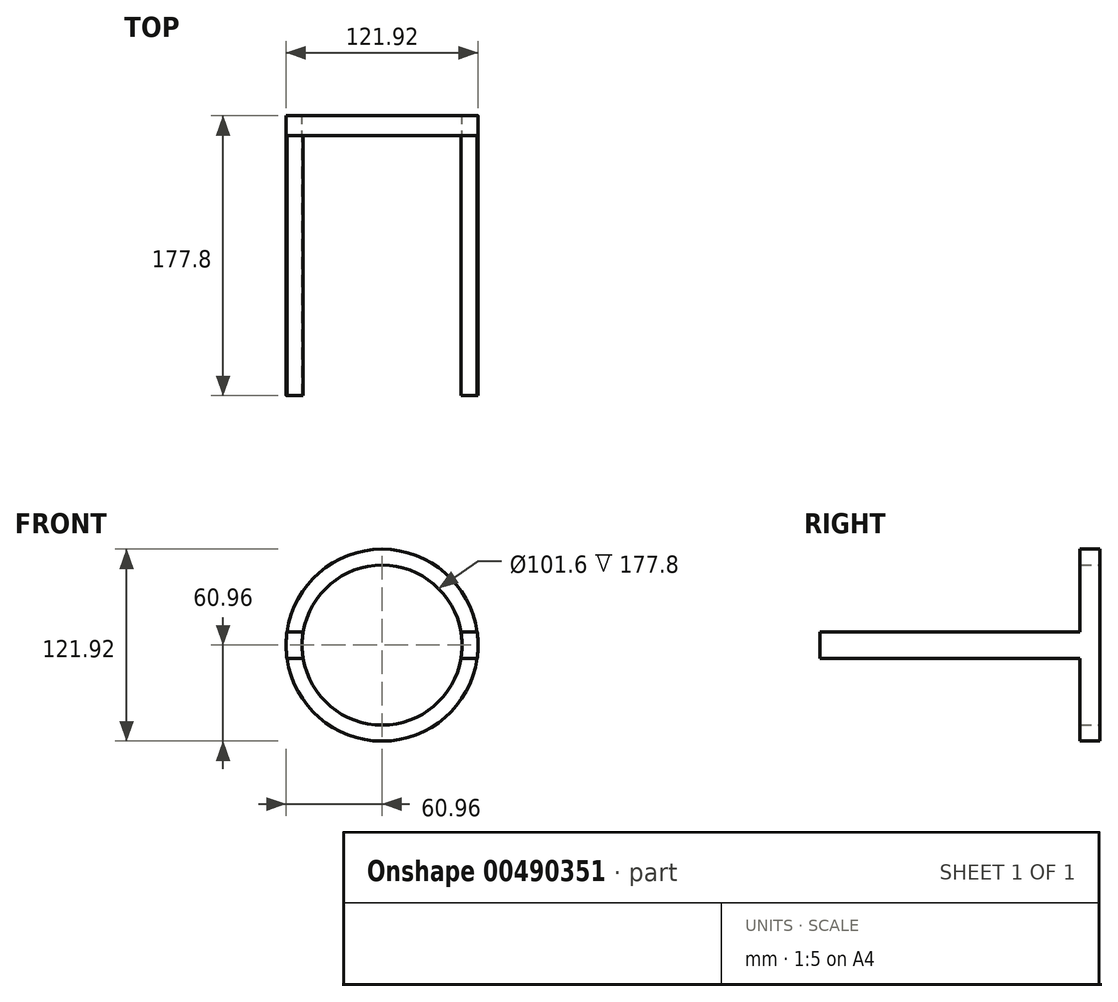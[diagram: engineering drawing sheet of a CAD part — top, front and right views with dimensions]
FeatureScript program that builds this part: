
annotation { "Feature Type Name" : "Feature", "Feature Type Description" : "" }
export const myFeature = defineFeature(function(context is Context, id is Id, definition is map)
    precondition{}
    {
        {
            var Q0;
            Q0=qCreatedBy(makeId("Front.planeOp"),FACE);
            var sketch = newSketch(context, id + "F0", { "sketchPlane" : qUnion([Q0])});
            skCircle(sketch, "E0", {"center": v(0, 0) * mm, "radius": 60.96 * mm});
            skCircle(sketch, "E1", {"center": v(0, 0) * mm, "radius": 50.8 * mm});
            skLineSegment(sketch, "E2", {"start": v(-60.37, 8.45) * mm, "end": v(-50.1, 8.45) * mm});
            skLineSegment(sketch, "E3", {"start": v(-60.37, -8.45) * mm, "end": v(-50.1, -8.45) * mm});
            skLineSegment(sketch, "E4", {"start": v(60.37, -8.45) * mm, "end": v(50.1, -8.45) * mm});
            skLineSegment(sketch, "E5", {"start": v(60.37, 8.45) * mm, "end": v(50.1, 8.45) * mm});
            skSolve(sketch);
        }
        {
            var Q0;
            {var subQ0=sQuery(id+"F0.wireOp",EDGE,"E2");Q0=makeQuery(id+"F0.imprint","IMPRINT",FACE,{"disambiguationData":[TD([[makeQuery(id+"F0.imprint","IMPRINT",EDGE,{"derivedFrom":subQ0}),-1.0]])]});}
            var Q1;
            {var subQ0=sQuery(id+"F0.wireOp",EDGE,"E4");Q1=makeQuery(id+"F0.imprint","IMPRINT",FACE,{"disambiguationData":[TD([[makeQuery(id+"F0.imprint","IMPRINT",EDGE,{"derivedFrom":subQ0}),-1.0]])]});}
            extrude(context, id + "F1", {"entities" : qUnion([Q0, Q1]), "depth" : 177.8 * mm});
        }
        {
            var Q0;
            {var subQ0=sQuery(id+"F0.wireOp",EDGE,"E2");Q0=makeQuery(id+"F0.imprint","IMPRINT",FACE,{"disambiguationData":[TD([[makeQuery(id+"F0.imprint","IMPRINT",EDGE,{"derivedFrom":subQ0}),1.0]])]});}
            var Q1;
            {var subQ0=sQuery(id+"F0.wireOp",EDGE,"E3");Q1=makeQuery(id+"F0.imprint","IMPRINT",FACE,{"disambiguationData":[TD([[makeQuery(id+"F0.imprint","IMPRINT",EDGE,{"derivedFrom":subQ0}),-1.0]])]});}
            extrude(context, id + "F2", {"entities" : qUnion([Q0, Q1]), "operationType" : NewBodyOperationType.ADD, "depth" : 12.7 * mm});
        }
    });
